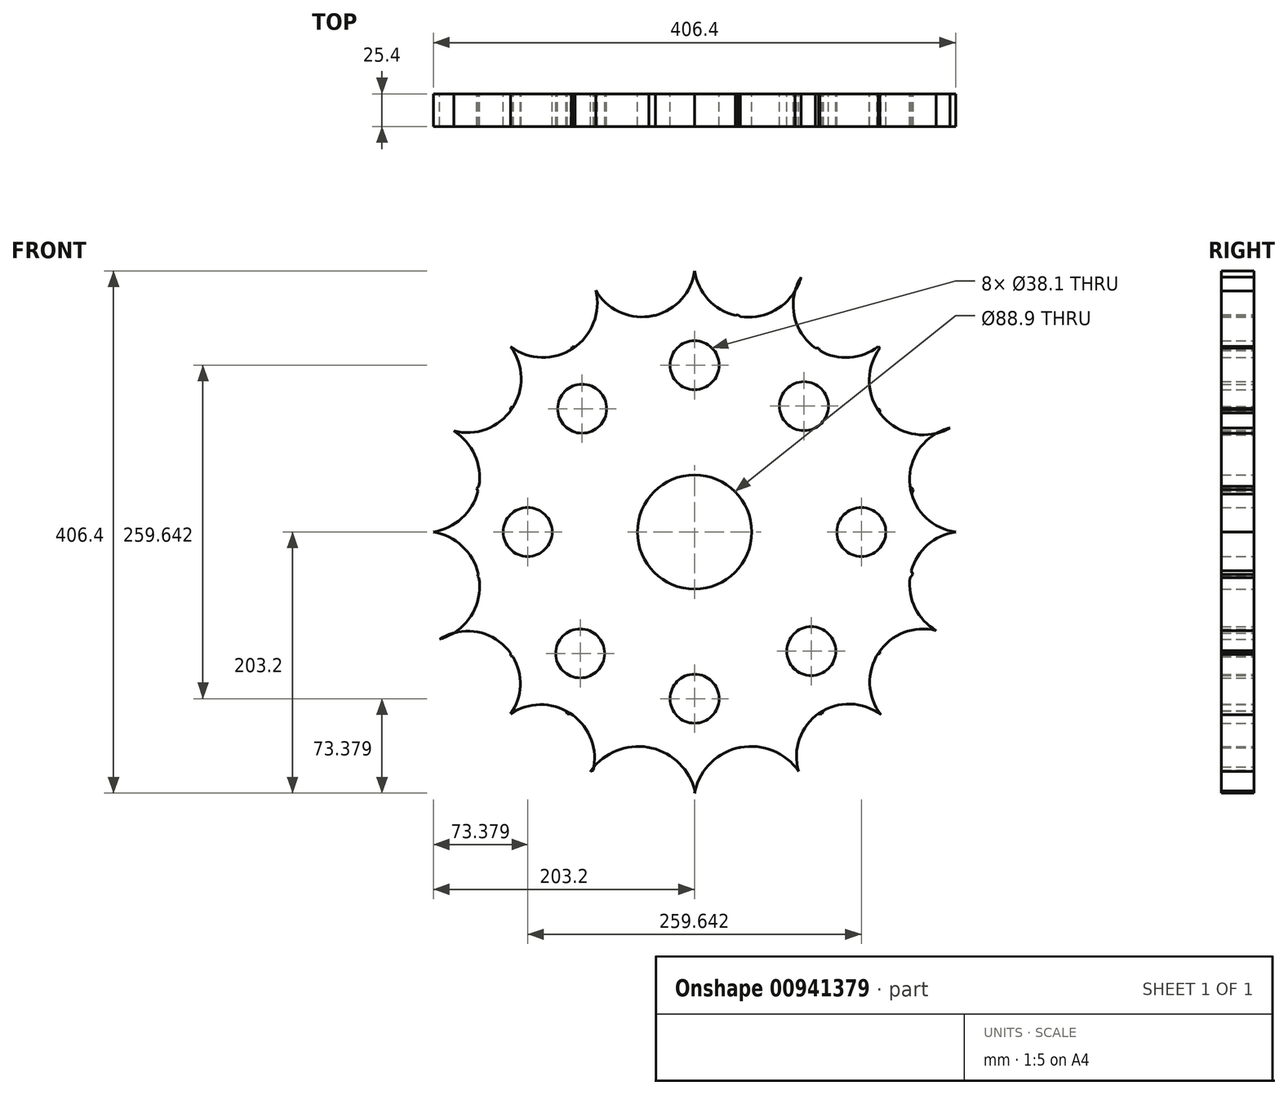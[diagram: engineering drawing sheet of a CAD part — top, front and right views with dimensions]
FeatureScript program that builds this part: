
annotation { "Feature Type Name" : "Feature", "Feature Type Description" : "" }
export const myFeature = defineFeature(function(context is Context, id is Id, definition is map)
    precondition{}
    {
        {
            var Q0;
            Q0=qCreatedBy(makeId("Front.planeOp"),FACE);
            var sketch = newSketch(context, id + "F0", { "sketchPlane" : qUnion([Q0])});
            skCircle(sketch, "E0", {"center": v(0, 0) * mm, "radius": 44.45 * mm});
            skArc(sketch, "E1", {"start": v(-167.74, 35.46) * mm, "mid": v(-168.14, 33.54) * mm, "end": v(-168.5, 31.62) * mm});
            skLineSegment(sketch, "E2", {"start": v(-35.4, -167.8) * mm, "end": v(-35.46, -167.74) * mm});
            skLineSegment(sketch, "E3", {"start": v(-169.39, 33.81) * mm, "end": v(-167.74, 35.46) * mm});
            skLineSegment(sketch, "E4", {"start": v(33.85, 169.35) * mm, "end": v(35.46, 167.74) * mm});
            skLineSegment(sketch, "E5", {"start": v(170.01, -33.19) * mm, "end": v(167.74, -35.46) * mm});
            skLineSegment(sketch, "E6", {"start": v(-144.43, -142.93) * mm, "end": v(-143.14, -141.64) * mm});
            skLineSegment(sketch, "E7", {"start": v(-143.14, 96.76) * mm, "end": v(-143.14, 94.37) * mm});
            skLineSegment(sketch, "E8", {"start": v(-98.95, -141.64) * mm, "end": v(-96.6, -141.64) * mm});
            skLineSegment(sketch, "E9", {"start": v(144.31, -141.64) * mm, "end": v(144.31, -141.4) * mm});
            skLineSegment(sketch, "E10", {"start": v(144.31, 143.05) * mm, "end": v(141.07, 143.06) * mm});
            skLineSegment(sketch, "E11", {"start": v(-40.99, 17.2) * mm, "end": v(-38.06, 15.97) * mm});
            skLineSegment(sketch, "E12", {"start": v(16.45, -37.85) * mm, "end": v(17.72, -40.77) * mm});
            skLineSegment(sketch, "E13", {"start": v(0, 0) * mm, "end": v(-1.29, 3.15) * mm});
            skLineSegment(sketch, "E14", {"start": v(0, 0) * mm, "end": v(17.1, 41.03) * mm});
            skLineSegment(sketch, "E15", {"start": v(-16.45, -37.85) * mm, "end": v(-17.72, -40.77) * mm});
            skLineSegment(sketch, "E16", {"start": v(0, 0) * mm, "end": v(3.2, -1.3) * mm});
            skLineSegment(sketch, "E17", {"start": v(0, 0) * mm, "end": v(-1.06, 0.44) * mm});
            skLineSegment(sketch, "E18", {"start": v(0, 0) * mm, "end": v(-2.59, -1.09) * mm});
            skLineSegment(sketch, "E19", {"start": v(0, 0) * mm, "end": v(1.34, 0.55) * mm});
            skLineSegment(sketch, "E20", {"start": v(144.31, 95.2) * mm, "end": v(141.92, 96.2) * mm});
            skLineSegment(sketch, "E21", {"start": v(-95.06, 144.03) * mm, "end": v(-95.83, 142.17) * mm});
            skLineSegment(sketch, "E22", {"start": v(-143.14, -96.38) * mm, "end": v(-141.3, -97.12) * mm});
            skLineSegment(sketch, "E23", {"start": v(99.2, -141.64) * mm, "end": v(100.24, -139.1) * mm});
            skLineSegment(sketch, "E24", {"start": v(144.31, -94.61) * mm, "end": v(142.48, -95.36) * mm});
            skLineSegment(sketch, "E25", {"start": v(-98.95, -141.64) * mm, "end": v(-99.86, -139.37) * mm});
            skLineSegment(sketch, "E26", {"start": v(-143.14, 96.76) * mm, "end": v(-140.9, 97.68) * mm});
            skLineSegment(sketch, "E27", {"start": v(96.64, 143.25) * mm, "end": v(97.59, 140.97) * mm});
            skLineSegment(sketch, "E28.trimOffspring", {"start": v(-143.14, -94.37) * mm, "end": v(-143.14, -96.38) * mm});
            skLineSegment(sketch, "E29.trimOffspring", {"start": v(-109.35, 110.62) * mm, "end": v(-109.04, 110.31) * mm});
            skLineSegment(sketch, "E30.trimOffspring", {"start": v(-168.5, 31.62) * mm, "end": v(-169.39, 33.81) * mm});
            skLineSegment(sketch, "E31.trimOffspring", {"start": v(-30.57, 32.27) * mm, "end": v(-28.31, 30.03) * mm});
            skLineSegment(sketch, "E32.trimOffspring", {"start": v(-93.02, 144.02) * mm, "end": v(-95.06, 144.03) * mm});
            skLineSegment(sketch, "E33.trimOffspring", {"start": v(-16.94, 41.1) * mm, "end": v(-15.73, 38.16) * mm});
            skLineSegment(sketch, "E34.trimOffspring", {"start": v(-44.45, 0) * mm, "end": v(-41.28, 0) * mm});
            skLineSegment(sketch, "E35.trimOffspring", {"start": v(-40.99, -17.2) * mm, "end": v(-38.06, -15.97) * mm});
            skLineSegment(sketch, "E36.trimOffspring", {"start": v(-32.17, -30.67) * mm, "end": v(-29.93, -28.43) * mm});
            skLineSegment(sketch, "E37.trimOffspring", {"start": v(-17.72, -40.77) * mm, "end": v(-16.45, -37.85) * mm});
            skLineSegment(sketch, "E38.trimOffspring", {"start": v(0, -153.38) * mm, "end": v(0, -153.84) * mm});
            skLineSegment(sketch, "E39.trimOffspring", {"start": v(17.72, -40.77) * mm, "end": v(16.45, -37.85) * mm});
            skLineSegment(sketch, "E40.trimOffspring", {"start": v(41.16, -16.8) * mm, "end": v(38.22, -15.6) * mm});
            skLineSegment(sketch, "E41.trimOffspring", {"start": v(41.16, 16.8) * mm, "end": v(38.22, 15.6) * mm});
            skLineSegment(sketch, "E42.trimOffspring", {"start": v(17.1, 41.03) * mm, "end": v(15.89, 38.1) * mm});
            skLineSegment(sketch, "E43.trimOffspring", {"start": v(0, 44.45) * mm, "end": v(0, 41.28) * mm});
            skLineSegment(sketch, "E44.trimOffspring", {"start": v(-168.31, -32.64) * mm, "end": v(-168.97, -34.23) * mm});
            skLineSegment(sketch, "E45.trimOffspring", {"start": v(-167.74, -35.46) * mm, "end": v(-168.97, -34.23) * mm});
            skLineSegment(sketch, "E46.trimOffspring", {"start": v(-35.34, -167.77) * mm, "end": v(-35.4, -167.8) * mm});
            skLineSegment(sketch, "E47.trimOffspring", {"start": v(96.6, -141.64) * mm, "end": v(99.2, -141.64) * mm});
            skLineSegment(sketch, "E48.trimOffspring", {"start": v(35.46, -167.74) * mm, "end": v(35.22, -167.98) * mm});
            skLineSegment(sketch, "E49.trimOffspring", {"start": v(34.9, -167.86) * mm, "end": v(35.22, -167.98) * mm});
            skLineSegment(sketch, "E50.trimOffspring", {"start": v(144.31, 92.57) * mm, "end": v(144.31, 95.2) * mm});
            skLineSegment(sketch, "E51.trimOffspring", {"start": v(168.9, 29.5) * mm, "end": v(170.28, 32.92) * mm});
            skLineSegment(sketch, "E52.trimOffspring", {"start": v(31.75, 168.49) * mm, "end": v(33.85, 169.35) * mm});
            skLineSegment(sketch, "E53.trimOffspring", {"start": v(-30.54, 168.7) * mm, "end": v(-33.32, 169.88) * mm});
            skLineSegment(sketch, "E54.trimOffspring", {"start": v(167.74, 35.46) * mm, "end": v(170.28, 32.92) * mm});
            skLineSegment(sketch, "E55.trimOffspring", {"start": v(141.56, 143.06) * mm, "end": v(142.93, 144.43) * mm});
            skLineSegment(sketch, "E56.trimOffspring", {"start": v(168.77, -30.2) * mm, "end": v(170.01, -33.19) * mm});
            skLineSegment(sketch, "E57.trimOffspring", {"start": v(144.31, -141.64) * mm, "end": v(145.02, -142.34) * mm});
            skArc(sketch, "E58.trimOffspring", {"start": v(144.31, 143.05) * mm, "mid": v(143.62, 143.74) * mm, "end": v(142.93, 144.43) * mm});
            skArc(sketch, "E59.trimOffspring", {"start": v(-140.9, 97.68) * mm, "mid": v(-142.03, 96.03) * mm, "end": v(-143.14, 94.37) * mm});
            skArc(sketch, "E60.trimOffspring", {"start": v(-93.02, 144.02) * mm, "mid": v(-94.43, 143.1) * mm, "end": v(-95.83, 142.17) * mm});
            skArc(sketch, "E61.trimOffspring", {"start": v(-30.54, 168.7) * mm, "mid": v(-33, 168.24) * mm, "end": v(-35.46, 167.74) * mm});
            skArc(sketch, "E62.trimOffspring", {"start": v(35.46, 167.74) * mm, "mid": v(33.6, 168.12) * mm, "end": v(31.75, 168.49) * mm});
            skArc(sketch, "E63.trimOffspring", {"start": v(97.59, 140.97) * mm, "mid": v(95.9, 142.12) * mm, "end": v(94.2, 143.26) * mm});
            skArc(sketch, "E64.trimOffspring", {"start": v(144.31, 92.57) * mm, "mid": v(143.13, 94.4) * mm, "end": v(141.92, 96.2) * mm});
            skArc(sketch, "E65.trimOffspring", {"start": v(168.9, 29.5) * mm, "mid": v(168.34, 32.48) * mm, "end": v(167.74, 35.46) * mm});
            skArc(sketch, "E66.trimOffspring", {"start": v(167.74, -35.46) * mm, "mid": v(168.28, -32.83) * mm, "end": v(168.77, -30.2) * mm});
            skArc(sketch, "E67.trimOffspring", {"start": v(142.48, -95.36) * mm, "mid": v(143.4, -93.97) * mm, "end": v(144.31, -92.57) * mm});
            skArc(sketch, "E68.trimOffspring", {"start": v(96.6, -141.64) * mm, "mid": v(98.43, -140.38) * mm, "end": v(100.24, -139.1) * mm});
            skArc(sketch, "E69.trimOffspring", {"start": v(34.9, -167.86) * mm, "mid": v(35.18, -167.8) * mm, "end": v(35.46, -167.74) * mm});
            skArc(sketch, "E70.trimOffspring", {"start": v(-35.46, -167.74) * mm, "mid": v(-35.4, -167.76) * mm, "end": v(-35.34, -167.77) * mm});
            skArc(sketch, "E71.trimOffspring", {"start": v(-99.86, -139.37) * mm, "mid": v(-98.24, -140.51) * mm, "end": v(-96.6, -141.64) * mm});
            skArc(sketch, "E72.trimOffspring", {"start": v(-143.14, -94.37) * mm, "mid": v(-142.22, -95.75) * mm, "end": v(-141.3, -97.12) * mm});
            skArc(sketch, "E73.trimOffspring", {"start": v(-168.31, -32.64) * mm, "mid": v(-168.03, -34.05) * mm, "end": v(-167.74, -35.46) * mm});
            skCircle(sketch, "E74", {"center": v(-129.82, 0) * mm, "radius": 19.05 * mm});
            skCircle(sketch, "E75", {"center": v(-87.47, 95.93) * mm, "radius": 19.05 * mm});
            skCircle(sketch, "E76", {"center": v(0, 129.82) * mm, "radius": 19.05 * mm});
            skCircle(sketch, "E77", {"center": v(85.18, 97.97) * mm, "radius": 19.05 * mm});
            skCircle(sketch, "E78", {"center": v(129.82, 0) * mm, "radius": 19.05 * mm});
            skCircle(sketch, "E79", {"center": v(90.8, -92.78) * mm, "radius": 19.05 * mm});
            skCircle(sketch, "E80", {"center": v(0, -129.82) * mm, "radius": 19.05 * mm});
            skCircle(sketch, "E81", {"center": v(-88.95, -94.56) * mm, "radius": 19.05 * mm});
            skCircle(sketch, "E82", {"center": v(0, 0) * mm, "radius": 41.28 * mm});
            skLineSegment(sketch, "E83.trimOffspring", {"start": v(1.07, 2.57) * mm, "end": v(0, 0) * mm});
            skLineSegment(sketch, "E84.trimOffspring", {"start": v(28.43, 29.93) * mm, "end": v(30.67, 32.17) * mm});
            skLineSegment(sketch, "E85.trimOffspring", {"start": v(38.22, 15.6) * mm, "end": v(41.16, 16.8) * mm});
            skLineSegment(sketch, "E86.trimOffspring", {"start": v(41.28, 0) * mm, "end": v(44.45, 0) * mm});
            skLineSegment(sketch, "E87.trimOffspring", {"start": v(1.34, 0.55) * mm, "end": v(0, 0) * mm});
            skLineSegment(sketch, "E88.trimOffspring", {"start": v(3.2, -1.3) * mm, "end": v(0, 0) * mm});
            skLineSegment(sketch, "E89.trimOffspring", {"start": v(30.19, -28.15) * mm, "end": v(32.44, -30.39) * mm});
            skLineSegment(sketch, "E90.trimOffspring", {"start": v(0, -41.28) * mm, "end": v(0, -44.45) * mm});
            skLineSegment(sketch, "E91.trimOffspring", {"start": v(38.22, -15.6) * mm, "end": v(41.16, -16.8) * mm});
            skLineSegment(sketch, "E92.trimOffspring", {"start": v(-2.59, -1.09) * mm, "end": v(1.07, 2.57) * mm});
            skLineSegment(sketch, "E93.trimOffspring", {"start": v(-2.59, -1.09) * mm, "end": v(0, 0) * mm});
            skLineSegment(sketch, "E94.trimOffspring", {"start": v(-1.5, 0) * mm, "end": v(1.88, 0) * mm});
            skLineSegment(sketch, "E95.trimOffspring", {"start": v(-1.06, 0.44) * mm, "end": v(0, 0) * mm});
            skLineSegment(sketch, "E96.trimOffspring", {"start": v(-1.3, 3.18) * mm, "end": v(3.2, -1.3) * mm});
            skLineSegment(sketch, "E97.trimOffspring", {"start": v(-38.06, 15.97) * mm, "end": v(-40.99, 17.2) * mm});
            skLineSegment(sketch, "E98.trimOffspring", {"start": v(-15.6, 38.22) * mm, "end": v(-16.8, 41.16) * mm});
            skLineSegment(sketch, "E99.trimOffspring", {"start": v(0, 1.87) * mm, "end": v(0, 0) * mm});
            skLineSegment(sketch, "E100.trimOffspring", {"start": v(-1.3, 3.18) * mm, "end": v(0, 0) * mm});
            skArc(sketch, "E101", {"start": v(-203.2, 0) * mm, "mid": v(-168.04, 33.82) * mm, "end": v(-187.38, 78.62) * mm});
            skArc(sketch, "E102", {"start": v(-187.38, 78.62) * mm, "mid": v(-142.1, 95.8) * mm, "end": v(-143.14, 144.22) * mm});
            skArc(sketch, "E103", {"start": v(-143.14, 144.22) * mm, "mid": v(-94.58, 142.94) * mm, "end": v(-76.77, 188.14) * mm});
            skArc(sketch, "E104", {"start": v(-76.77, 188.14) * mm, "mid": v(-32.99, 168.15) * mm, "end": v(0, 203.2) * mm});
            skArc(sketch, "E105", {"start": v(0, 203.2) * mm, "mid": v(39.5, 167.31) * mm, "end": v(82.92, 198.37) * mm});
            skArc(sketch, "E106", {"start": v(82.92, 198.37) * mm, "mid": v(90.37, 146.3) * mm, "end": v(142.93, 144.43) * mm});
            skArc(sketch, "E107", {"start": v(144.31, 143.05) * mm, "mid": v(146.48, 89.9) * mm, "end": v(198.94, 81.03) * mm});
            skArc(sketch, "E108", {"start": v(198.94, 81.03) * mm, "mid": v(167.34, 38.74) * mm, "end": v(203.2, 0) * mm});
            skArc(sketch, "E109", {"start": v(203.2, 0) * mm, "mid": v(168.15, -32.99) * mm, "end": v(188.14, -76.77) * mm});
            skArc(sketch, "E110", {"start": v(188.14, -76.77) * mm, "mid": v(143.2, -94.18) * mm, "end": v(145.02, -142.34) * mm});
            skArc(sketch, "E111", {"start": v(145.02, -142.34) * mm, "mid": v(97.02, -141.1) * mm, "end": v(81, -186.36) * mm});
            skArc(sketch, "E112", {"start": v(81, -186.36) * mm, "mid": v(34.9, -167.86) * mm, "end": v(0, -203.2) * mm});
            skArc(sketch, "E113", {"start": v(0.55, -202.65) * mm, "mid": v(-34.9, -167.85) * mm, "end": v(-81, -186.36) * mm});
            skPoint(sketch, "E113.first.point", {"position": v(0.53, -202.54) * mm});
            skArc(sketch, "E114", {"start": v(-78.77, -185.46) * mm, "mid": v(-96.06, -141.67) * mm, "end": v(-143.14, -141.64) * mm});
            skPoint(sketch, "E114.first.point", {"position": v(-78.6, -184.64) * mm});
            skArc(sketch, "E115", {"start": v(-143.14, -141.64) * mm, "mid": v(-146.84, -89.87) * mm, "end": v(-198.35, -83.48) * mm});
            skArc(sketch, "E116", {"start": v(-198.35, -83.48) * mm, "mid": v(-167.29, -39.8) * mm, "end": v(-203.2, 0) * mm});
            skLineSegment(sketch, "E117.trimOffspring", {"start": v(96.64, 143.25) * mm, "end": v(94.2, 143.26) * mm});
            skPoint(sketch, "E118.orphan", {"position": v(203.2, 0) * mm});
            skLineSegment(sketch, "E119.trimOffspring", {"start": v(144.31, -94.61) * mm, "end": v(144.31, -92.57) * mm});
            skLineSegment(sketch, "E120.trimOffspring", {"start": v(144.08, -141.64) * mm, "end": v(144.31, -141.64) * mm});
            skLineSegment(sketch, "E121.trimOffspring", {"start": v(0.55, -202.65) * mm, "end": v(0, -203.2) * mm});
            skLineSegment(sketch, "E122.trimOffspring", {"start": v(-78.77, -185.46) * mm, "end": v(-81, -186.36) * mm});
            skSolve(sketch);
        }
        {
            var Q0;
            Q0 = qSketchRegion(id + "F0", true);
            extrude(context, id + "F1", {"entities" : qUnion([Q0]), "depth" : 25.4 * mm, "offsetDistance" : 25.4 * mm});
        }
    });
